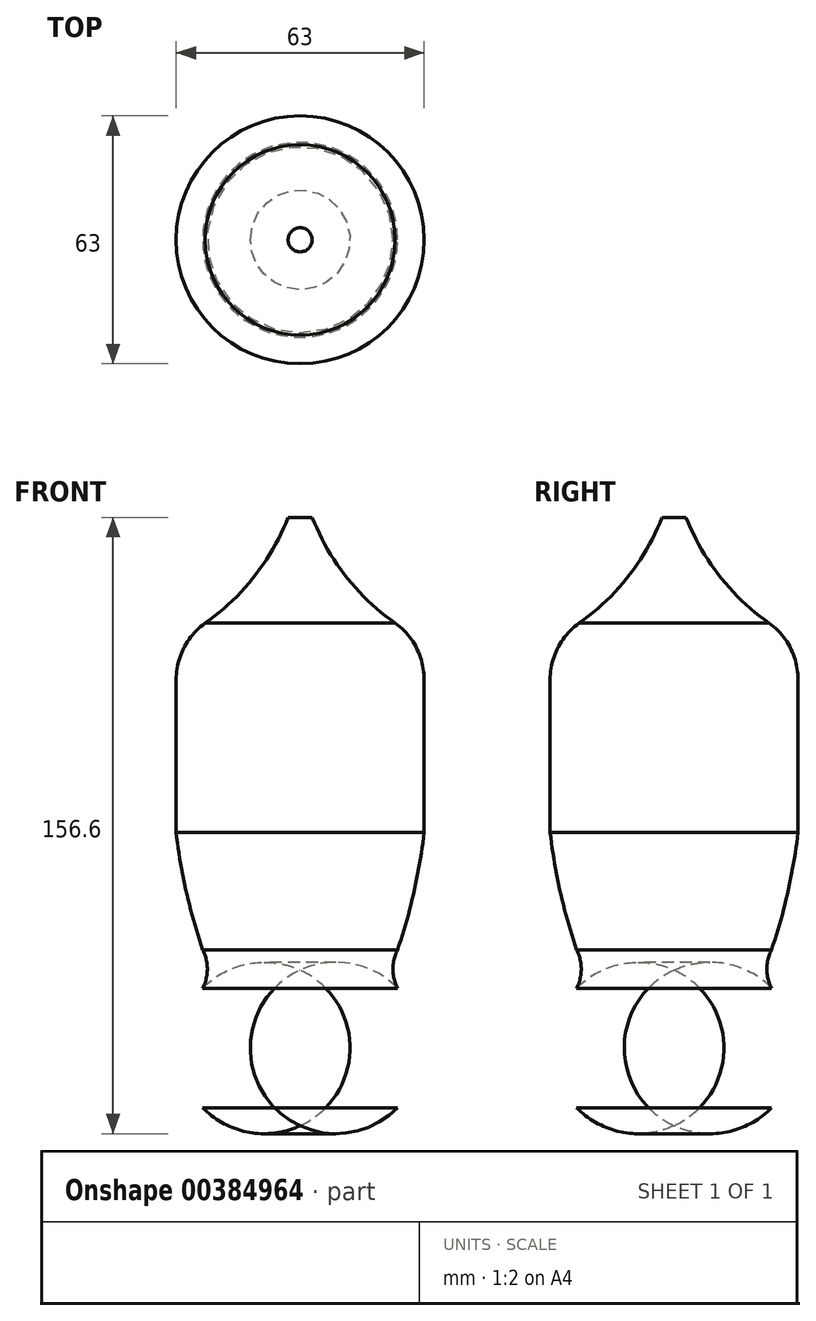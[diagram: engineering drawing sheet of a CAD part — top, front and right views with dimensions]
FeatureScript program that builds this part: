
annotation { "Feature Type Name" : "Feature", "Feature Type Description" : "" }
export const myFeature = defineFeature(function(context is Context, id is Id, definition is map)
    precondition{}
    {
        {
            var Q0;
            Q0=qCreatedBy(makeId("Front.planeOp"),FACE);
            var sketch = newSketch(context, id + "F0", { "sketchPlane" : qUnion([Q0])});
            skLineSegment(sketch, "E0", {"start": v(0, 79.7) * mm, "end": v(0, -76.67) * mm});
            skLineSegment(sketch, "E1", {"start": v(0, -76.67) * mm, "end": v(24.74, -76.67) * mm});
            skArc(sketch, "E2", {"start": v(24.74, -76.67) * mm, "mid": v(30.9, -61.49) * mm, "end": v(24.74, -46.3) * mm});
            skArc(sketch, "E3", {"start": v(24.74, -36.59) * mm, "mid": v(23.58, -41.45) * mm, "end": v(24.74, -46.3) * mm});
            skArc(sketch, "E4", {"start": v(24.74, -36.59) * mm, "mid": v(28.92, -21.82) * mm, "end": v(31.5, -6.7) * mm});
            skLineSegment(sketch, "E5", {"start": v(31.5, -6.7) * mm, "end": v(31.5, 32.03) * mm});
            skArc(sketch, "E6", {"start": v(31.5, 32.03) * mm, "mid": v(29.56, 40.13) * mm, "end": v(24.14, 46.47) * mm});
            skArc(sketch, "E7", {"start": v(3.06, 73.33) * mm, "mid": v(11.61, 58.34) * mm, "end": v(24.14, 46.47) * mm});
            skLineSegment(sketch, "E8", {"start": v(3.06, 73.33) * mm, "end": v(0, 73.33) * mm});
            skLineSegment(sketch, "E9", {"start": v(0, 73.33) * mm, "end": v(0, -76.67) * mm});
            skSolve(sketch);
        }
        {
            var Q0;
            Q0=makeQuery(id+"F0.imprint","IMPRINT",FACE,{"disambiguationData":[TD([[makeQuery(id+"F0.imprint","IMPRINT",EDGE,{"derivedFrom":sQuery(id+"F0.wireOp",EDGE,"E1")}),1.0]])]});
            var Q1;
            Q1=sQuery(id+"F0.wireOp",EDGE,"E0");
            revolve(context, id + "F1", {"entities" : qUnion([Q0]), "axis" : qUnion([Q1]), "revolveType" : RevolveType.FULL});
        }
    });
